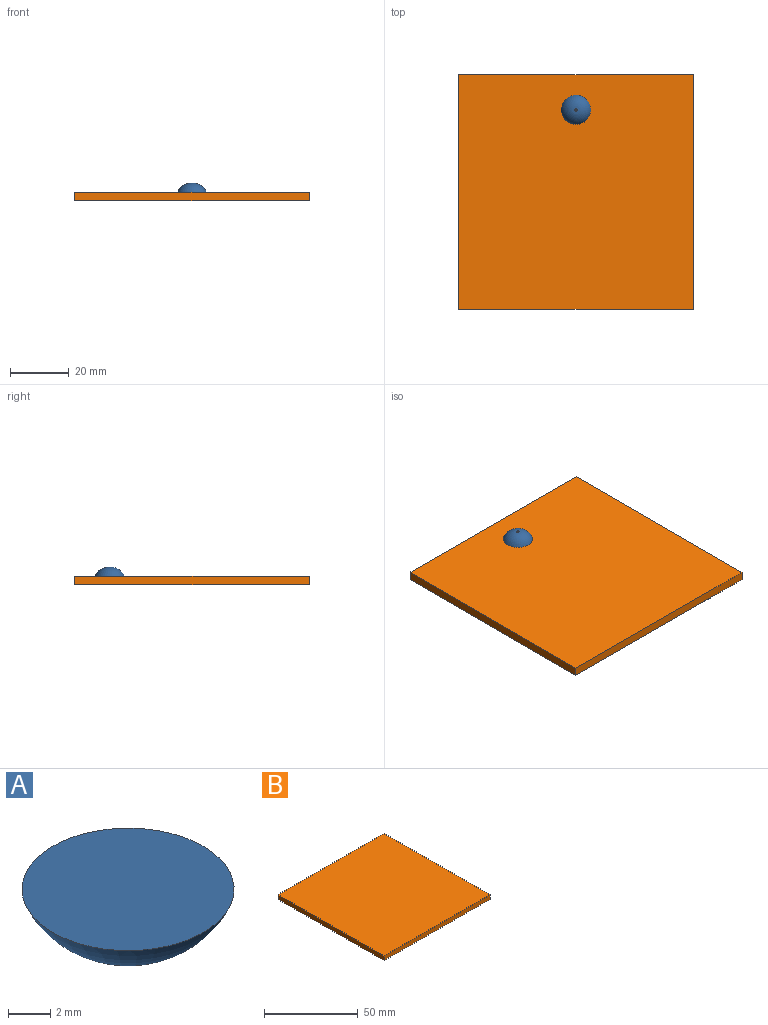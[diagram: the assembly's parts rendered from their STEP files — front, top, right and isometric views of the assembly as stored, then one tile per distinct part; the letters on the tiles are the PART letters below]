
ASSEMBLY  parts=2 mates=1
PART A: 3 faces, bbox 10x10x3 mm
  f0: plane 0.84x0.84mm, normal (0,0,-1), area 0.5mm2, adj f2
  f1: plane 10x10mm, normal (0,0,1), area 78.5mm2, adj f2
  f2: torus R=0.42mm, axis (0,0,-1), area 109.5mm2, adj f0,f1
PART B: 6 faces, bbox 80x80x3 mm
  f0: plane 80x3mm, normal (0,-1,0), area 240mm2, adj f1,f3,f4,f5
  f1: plane 80x3mm, normal (1,0,0), area 240mm2, adj f0,f2,f4,f5
  f2: plane 80x3mm, normal (0,1,0), area 240mm2, adj f1,f3,f4,f5
  f3: plane 80x3mm, normal (-1,0,0), area 240mm2, adj f0,f2,f4,f5
  f4: plane 80x80mm, normal (0,0,1), area 6400mm2, adj f0,f1,f2,f3
  f5: plane 80x80mm, normal (0,0,-1), area 6400mm2, adj f0,f1,f2,f3
PLACE A rot(axis=(1,0,0),180deg) t=(0,136,26)mm
PLACE B rot(axis=(0,1,0),180deg) t=(-80,0,26)mm
MATE fastened A.f2 <-> B.f5  axis (0,0,-1) through (-40,68,26)mm
